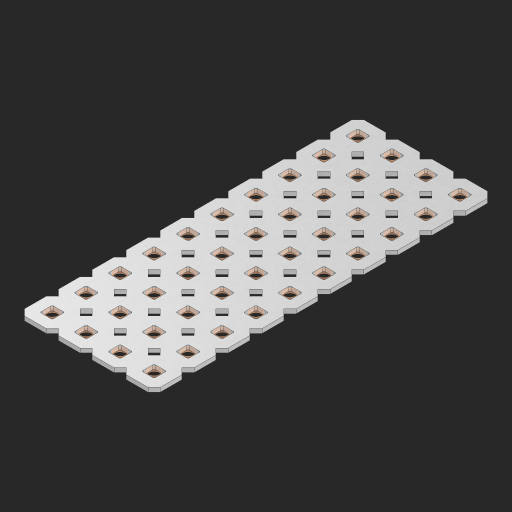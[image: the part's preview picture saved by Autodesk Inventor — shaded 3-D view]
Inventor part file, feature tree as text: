
AUTODESK INVENTOR PART (.ipt)
format: ipt  version: 2023 (Build 270158000, 158)  size: 756,224 bytes
history: native  units: in
note: dims shown in document units (in); Inventor stores cm internally (conversion verified against a paired STEP export)
features: other x41, extrude x39, sketch x2, pattern_linear x1
ambient origin geometry x8: Origin, YZ Plane, XZ Plane, XY Plane, X Axis, Y Axis, Z Axis, Center Point
bodies: Solid1 (feature_tree), Body (feature_tree)
feature tree (83):
  pattern_linear  "Rectangular Pattern1"  Spacing1=0.09in  [1 undecoded]
  sketch  "Sketch1"  dims[d1=0.5in]
  sketch  "Sketch2"  dims[d2=0.182in d3=0.09in d4=0.09in d5=0.09in d6=0.09in d7=0.09in d8=0.09in d9=0.09in d10=0.09in d11=0.02in d13=0.0in d14=0.172in d15=0.0625in d16=0.0in d19=0.5in d22=0.5in]
  other  "Srf1"
  other  "Srf126"
  other  "Srf127"
  other  "Srf128"
  other  "Srf129"
  other  "Srf130"
  other  "Srf131"
  other  "Srf250"
  other  "Srf251"
  other  "Srf252"
  other  "Srf268"
  other  "Srf269"
  other  "Srf270"
  other  "Srf271"
  other  "Srf272"
  other  "Srf273"
  other  "Srf274"
  other  "Srf275"
  other  "Srf276"
  other  "Srf277"
  other  "Srf293"
  other  "Srf294"
  other  "Srf295"
  other  "Srf296"
  other  "Srf297"
  other  "Srf298"
  other  "Srf299"
  other  "Srf300"
  other  "Srf301"
  other  "Srf302"
  other  "Srf318"
  other  "Srf319"
  other  "Srf320"
  other  "Srf321"
  other  "Srf322"
  other  "Srf323"
  other  "Srf324"
  other  "Srf325"
  other  "Srf326"
  other  "Srf327"
  other  "Circle"
  extrude  "ExtrusionSrf126"  Depth=0.09in
  extrude  "ExtrusionSrf127"  Depth=0.09in
  extrude  "ExtrusionSrf128"  Depth=0.09in
  extrude  "ExtrusionSrf129"  Depth=0.09in
  extrude  "ExtrusionSrf130"  Depth=0.09in
  extrude  "ExtrusionSrf131"  Depth=0.09in
  extrude  "ExtrusionSrf250"  Depth=0.09in
  extrude  "ExtrusionSrf251"  Depth=0.02in
  extrude  "ExtrusionSrf252"  TaperAngle=0.0deg  [1 undecoded]
  extrude  "ExtrusionSrf268"  Depth=0.5in
  extrude  "ExtrusionSrf269"  Depth=0.0625in TaperAngle=0.0deg
  extrude  "ExtrusionSrf270"  Depth=0.5in
  extrude  "ExtrusionSrf271"  Depth=0.5in
  extrude  "ExtrusionSrf272"  [1 undecoded]
  extrude  "ExtrusionSrf273"  [1 undecoded]
  extrude  "ExtrusionSrf274"  [1 undecoded]
  extrude  "ExtrusionSrf275"  [1 undecoded]
  extrude  "ExtrusionSrf276"  [1 undecoded]
  extrude  "ExtrusionSrf277"  [1 undecoded]
  extrude  "ExtrusionSrf293"  [1 undecoded]
  extrude  "ExtrusionSrf294"  [1 undecoded]
  extrude  "ExtrusionSrf295"  [1 undecoded]
  extrude  "ExtrusionSrf296"  [1 undecoded]
  extrude  "ExtrusionSrf297"  [1 undecoded]
  extrude  "ExtrusionSrf298"  [1 undecoded]
  extrude  "ExtrusionSrf299"  [1 undecoded]
  extrude  "ExtrusionSrf300"  [1 undecoded]
  extrude  "ExtrusionSrf301"  [1 undecoded]
  extrude  "ExtrusionSrf302"  [1 undecoded]
  extrude  "ExtrusionSrf318"  [1 undecoded]
  extrude  "ExtrusionSrf319"  [1 undecoded]
  extrude  "ExtrusionSrf320"  [1 undecoded]
  extrude  "ExtrusionSrf321"  [1 undecoded]
  extrude  "ExtrusionSrf322"  [1 undecoded]
  extrude  "ExtrusionSrf323"  [1 undecoded]
  extrude  "ExtrusionSrf324"  [1 undecoded]
  extrude  "ExtrusionSrf325"  [1 undecoded]
  extrude  "ExtrusionSrf326"  [1 undecoded]
  extrude  "ExtrusionSrf327"  [1 undecoded]
note: 28 required parameter values undecoded (feature->parameter linkage not recoverable at this tier; creation-order binding heuristic only, values carry confidence <= 0.55)
